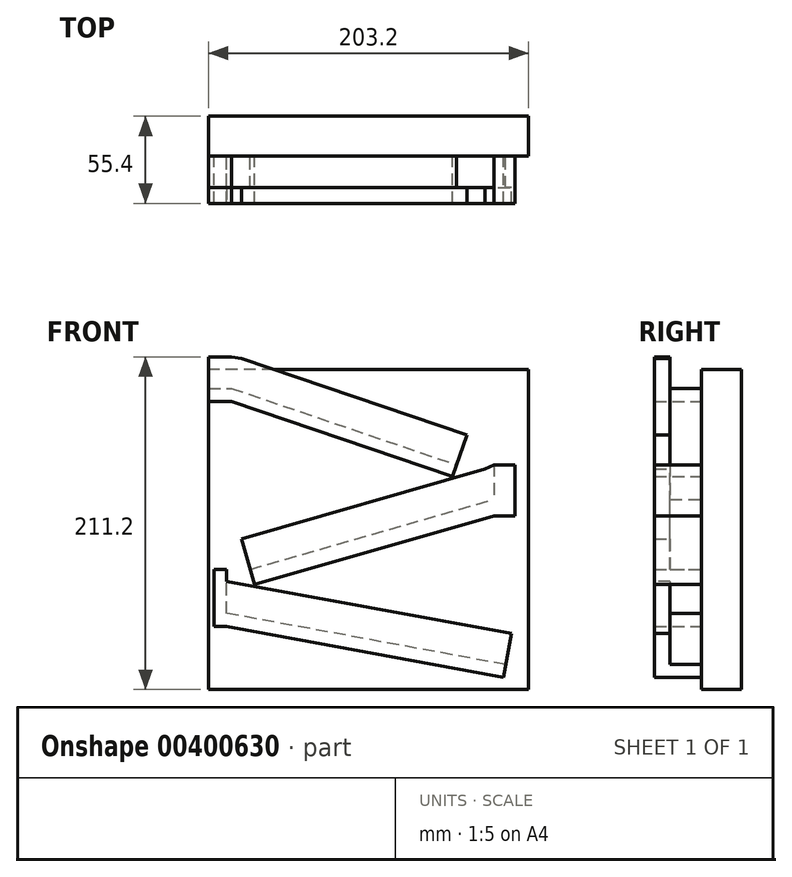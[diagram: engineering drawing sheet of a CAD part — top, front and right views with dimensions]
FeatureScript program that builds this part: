
annotation { "Feature Type Name" : "Feature", "Feature Type Description" : "" }
export const myFeature = defineFeature(function(context is Context, id is Id, definition is map)
    precondition{}
    {
        {
            var Q0;
            Q0=qCreatedBy(makeId("Front.planeOp"),FACE);
            var sketch = newSketch(context, id + "F0", { "sketchPlane" : qUnion([Q0])});
            skLineSegment(sketch, "E0.bottom", {"start": v(101.6, 101.6) * mm, "end": v(-101.6, 101.6) * mm});
            skLineSegment(sketch, "E0.top", {"start": v(101.6, -101.6) * mm, "end": v(-101.6, -101.6) * mm});
            skLineSegment(sketch, "E0.left", {"start": v(101.6, 101.6) * mm, "end": v(101.6, -101.6) * mm});
            skLineSegment(sketch, "E0.right", {"start": v(-101.6, 101.6) * mm, "end": v(-101.6, -101.6) * mm});
            skPoint(sketch, "E0.middle", {"position": v(0, 0) * mm});
            skSolve(sketch);
        }
        {
            var Q0;
            Q0 = qSketchRegion(id + "F0", true);
            extrude(context, id + "F1", {"entities" : qUnion([Q0]), "depth" : 25.4 * mm, "symmetric" : true});
        }
        {
            var Q0;
            Q0=makeQuery(id+"F1.opExtrude","CAP_FACE",FACE,{"disambiguationData":[OSD([sQuery(id+"F0.wireOp",EDGE,"E0.bottom"),sQuery(id+"F0.wireOp",EDGE,"E0.top"),sQuery(id+"F0.wireOp",EDGE,"E0.left"),sQuery(id+"F0.wireOp",EDGE,"E0.right")])],"isStart":false});
            var sketch = newSketch(context, id + "F2", { "sketchPlane" : qUnion([Q0])});
            skLineSegment(sketch, "E1", {"start": v(-101.6, 89.6) * mm, "end": v(-86.97, 89.6) * mm});
            skLineSegment(sketch, "E2", {"start": v(-86.97, 89.6) * mm, "end": v(55.97, 41) * mm});
            skLineSegment(sketch, "E3", {"start": v(55.97, 41) * mm, "end": v(53.43, 33.51) * mm});
            skLineSegment(sketch, "E4", {"start": v(53.43, 33.51) * mm, "end": v(-86.97, 81.26) * mm});
            skLineSegment(sketch, "E5", {"start": v(-86.97, 81.26) * mm, "end": v(-101.6, 81.26) * mm});
            skLineSegment(sketch, "E6", {"start": v(-101.6, 81.26) * mm, "end": v(-101.6, 89.6) * mm});
            skLineSegment(sketch, "E7", {"start": v(79.53, 41) * mm, "end": v(79.53, 8.54) * mm});
            skLineSegment(sketch, "E8", {"start": v(79.53, 8.54) * mm, "end": v(92.93, 8.54) * mm});
            skLineSegment(sketch, "E9", {"start": v(92.93, 8.54) * mm, "end": v(92.93, 41) * mm});
            skLineSegment(sketch, "E10", {"start": v(92.93, 41) * mm, "end": v(79.53, 41) * mm});
            skLineSegment(sketch, "E11", {"start": v(79.53, 8.54) * mm, "end": v(-72.35, -35.08) * mm});
            skLineSegment(sketch, "E12", {"start": v(-72.35, -35.08) * mm, "end": v(-75.13, -25.4) * mm});
            skLineSegment(sketch, "E13", {"start": v(-75.13, -25.4) * mm, "end": v(79.53, 19.02) * mm});
            skLineSegment(sketch, "E14", {"start": v(-98, -25.4) * mm, "end": v(-98, -61.62) * mm});
            skLineSegment(sketch, "E15", {"start": v(-98, -61.62) * mm, "end": v(-90.13, -61.62) * mm});
            skLineSegment(sketch, "E16", {"start": v(-90.13, -61.62) * mm, "end": v(-90.13, -25.4) * mm});
            skLineSegment(sketch, "E17", {"start": v(-90.13, -25.4) * mm, "end": v(-98, -25.4) * mm});
            skLineSegment(sketch, "E18", {"start": v(-90.13, -61.62) * mm, "end": v(85.66, -93.94) * mm});
            skLineSegment(sketch, "E19", {"start": v(85.66, -93.94) * mm, "end": v(87.14, -85.9) * mm});
            skLineSegment(sketch, "E20", {"start": v(87.14, -85.9) * mm, "end": v(-90.13, -53.3) * mm});
            skSolve(sketch);
        }
        {
            var Q0;
            Q0 = qSketchRegion(id + "F2", true);
            extrude(context, id + "F3", {"entities" : qUnion([Q0]), "operationType" : NewBodyOperationType.ADD, "depth" : 30 * mm});
        }
        {
            var Q0;
            Q0=makeQuery(id+"F3.opExtrude","SWEPT_FACE",FACE,{"disambiguationData":[OSD([sQuery(id+"F2.wireOp",EDGE,"E1")])]});
            var sketch = newSketch(context, id + "F4", { "sketchPlane" : qUnion([Q0])});
            skLineSegment(sketch, "E21.bottom", {"start": v(-101.6, -42.7) * mm, "end": v(-86.97, -42.7) * mm});
            skLineSegment(sketch, "E21.top", {"start": v(-101.6, -32.7) * mm, "end": v(-86.97, -32.7) * mm});
            skLineSegment(sketch, "E21.left", {"start": v(-101.6, -42.7) * mm, "end": v(-101.6, -32.7) * mm});
            skLineSegment(sketch, "E21.right", {"start": v(-86.97, -42.7) * mm, "end": v(-86.97, -32.7) * mm});
            skSolve(sketch);
        }
        {
            var Q0;
            Q0 = qSketchRegion(id + "F4", true);
            extrude(context, id + "F5", {"entities" : qUnion([Q0]), "operationType" : NewBodyOperationType.ADD, "depth" : 20 * mm});
        }
        {
            var Q0;
            Q0=makeQuery(id+"F3.opExtrude","SWEPT_FACE",FACE,{"disambiguationData":[OSD([sQuery(id+"F2.wireOp",EDGE,"E2")])]});
            var sketch = newSketch(context, id + "F6", { "sketchPlane" : qUnion([Q0])});
            skLineSegment(sketch, "E22.bottom", {"start": v(-111.2, -42.7) * mm, "end": v(39.79, -42.7) * mm});
            skLineSegment(sketch, "E22.top", {"start": v(-111.2, -32.7) * mm, "end": v(39.79, -32.7) * mm});
            skLineSegment(sketch, "E22.left", {"start": v(-111.2, -42.7) * mm, "end": v(-111.2, -32.7) * mm});
            skLineSegment(sketch, "E22.right", {"start": v(39.79, -42.7) * mm, "end": v(39.79, -32.7) * mm});
            skSolve(sketch);
        }
        {
            var Q0;
            Q0 = qSketchRegion(id + "F6", true);
            extrude(context, id + "F7", {"entities" : qUnion([Q0]), "operationType" : NewBodyOperationType.ADD, "depth" : 20 * mm});
        }
        {
            var Q0;
            Q0=makeQuery(id+"F7.boolean.opBoolean","MERGE",FACE,{"derivedFrom":[makeQuery(id+"F5.boolean.opBoolean","MERGE",FACE,{"derivedFrom":[makeQuery(id+"F3.opExtrude","CAP_FACE",FACE,{"disambiguationData":[OSD([sQuery(id+"F2.wireOp",EDGE,"E1"),sQuery(id+"F2.wireOp",EDGE,"E2"),sQuery(id+"F2.wireOp",EDGE,"E3"),sQuery(id+"F2.wireOp",EDGE,"E4"),sQuery(id+"F2.wireOp",EDGE,"E5"),sQuery(id+"F2.wireOp",EDGE,"E6")])],"isStart":false}),makeQuery(id+"F5.opExtrude","SWEPT_FACE",FACE,{"disambiguationData":[OSD([sQuery(id+"F4.wireOp",EDGE,"E21.bottom")])]})]}),makeQuery(id+"F7.opExtrude","SWEPT_FACE",FACE,{"disambiguationData":[OSD([sQuery(id+"F6.wireOp",EDGE,"E22.bottom")])]})]});
            var sketch = newSketch(context, id + "F8", { "sketchPlane" : qUnion([Q0])});
            skLineSegment(sketch, "E23", {"start": v(-86.97, 89.6) * mm, "end": v(-80.53, 108.54) * mm});
            skLineSegment(sketch, "E24", {"start": v(-80.53, 108.54) * mm, "end": v(-86.97, 109.6) * mm});
            skLineSegment(sketch, "E25", {"start": v(-86.97, 109.6) * mm, "end": v(-86.97, 89.6) * mm});
            skSolve(sketch);
        }
        {
            var Q0;
            Q0 = qSketchRegion(id + "F8", true);
            extrude(context, id + "F9", {"entities" : qUnion([Q0]), "operationType" : NewBodyOperationType.ADD, "oppositeDirection" : true, "depth" : 10 * mm});
        }
        {
            var Q0;
            Q0=makeQuery(id+"F3.opExtrude","SWEPT_FACE",FACE,{"disambiguationData":[OSD([sQuery(id+"F2.wireOp",EDGE,"E13")])]});
            var sketch = newSketch(context, id + "F10", { "sketchPlane" : qUnion([Q0])});
            skLineSegment(sketch, "E26.bottom", {"start": v(-79.22, -42.7) * mm, "end": v(81.69, -42.7) * mm});
            skLineSegment(sketch, "E26.top", {"start": v(-79.22, -32.7) * mm, "end": v(81.69, -32.7) * mm});
            skLineSegment(sketch, "E26.left", {"start": v(-79.22, -42.7) * mm, "end": v(-79.22, -32.7) * mm});
            skLineSegment(sketch, "E26.right", {"start": v(81.69, -42.7) * mm, "end": v(81.69, -32.7) * mm});
            skSolve(sketch);
        }
        {
            var Q0;
            Q0 = qSketchRegion(id + "F10", true);
            extrude(context, id + "F11", {"entities" : qUnion([Q0]), "operationType" : NewBodyOperationType.ADD, "depth" : 20 * mm});
        }
        {
            var Q0;
            Q0=makeQuery(id+"F3.opExtrude","SWEPT_FACE",FACE,{"disambiguationData":[OSD([sQuery(id+"F2.wireOp",EDGE,"E20")])]});
            var sketch = newSketch(context, id + "F12", { "sketchPlane" : qUnion([Q0])});
            skLineSegment(sketch, "E27.bottom", {"start": v(-79, -42.7) * mm, "end": v(101.23, -42.7) * mm});
            skLineSegment(sketch, "E27.top", {"start": v(-79, -32.7) * mm, "end": v(101.23, -32.7) * mm});
            skLineSegment(sketch, "E27.left", {"start": v(-79, -42.7) * mm, "end": v(-79, -32.7) * mm});
            skLineSegment(sketch, "E27.right", {"start": v(101.23, -42.7) * mm, "end": v(101.23, -32.7) * mm});
            skSolve(sketch);
        }
        {
            var Q0;
            Q0 = qSketchRegion(id + "F12", true);
            extrude(context, id + "F13", {"entities" : qUnion([Q0]), "operationType" : NewBodyOperationType.ADD, "depth" : 20 * mm});
        }
        {
            var Q0;
            Q0=makeQuery(id+"F11.boolean.opBoolean","MERGE",FACE,{"derivedFrom":[makeQuery(id+"F3.opExtrude","CAP_FACE",FACE,{"disambiguationData":[OSD([sQuery(id+"F2.wireOp",EDGE,"E7"),sQuery(id+"F2.wireOp",EDGE,"E8"),sQuery(id+"F2.wireOp",EDGE,"E9"),sQuery(id+"F2.wireOp",EDGE,"E10"),sQuery(id+"F2.wireOp",EDGE,"E11"),sQuery(id+"F2.wireOp",EDGE,"E12"),sQuery(id+"F2.wireOp",EDGE,"E13")])],"isStart":false}),makeQuery(id+"F11.opExtrude","SWEPT_FACE",FACE,{"disambiguationData":[OSD([sQuery(id+"F10.wireOp",EDGE,"E26.bottom")])]})]});
            var sketch = newSketch(context, id + "F14", { "sketchPlane" : qUnion([Q0])});
            skLineSegment(sketch, "E28", {"start": v(79.53, 19.02) * mm, "end": v(79.53, 41) * mm});
            skLineSegment(sketch, "E29", {"start": v(79.53, 41) * mm, "end": v(74, 38.24) * mm});
            skLineSegment(sketch, "E30", {"start": v(74, 38.24) * mm, "end": v(79.53, 19.02) * mm});
            skSolve(sketch);
        }
        {
            var Q0;
            Q0 = qSketchRegion(id + "F14", true);
            extrude(context, id + "F15", {"entities" : qUnion([Q0]), "operationType" : NewBodyOperationType.ADD, "oppositeDirection" : true, "depth" : 10 * mm});
        }
        {
            var Q0;
            Q0=makeQuery(id+"F13.boolean.opBoolean","MERGE",FACE,{"derivedFrom":[makeQuery(id+"F3.opExtrude","CAP_FACE",FACE,{"disambiguationData":[OSD([sQuery(id+"F2.wireOp",EDGE,"E14"),sQuery(id+"F2.wireOp",EDGE,"E15"),sQuery(id+"F2.wireOp",EDGE,"E16"),sQuery(id+"F2.wireOp",EDGE,"E17"),sQuery(id+"F2.wireOp",EDGE,"E18"),sQuery(id+"F2.wireOp",EDGE,"E19"),sQuery(id+"F2.wireOp",EDGE,"E20")])],"isStart":false}),makeQuery(id+"F13.opExtrude","SWEPT_FACE",FACE,{"disambiguationData":[OSD([sQuery(id+"F12.wireOp",EDGE,"E27.bottom")])]})]});
            var sketch = newSketch(context, id + "F16", { "sketchPlane" : qUnion([Q0])});
            skLineSegment(sketch, "E31", {"start": v(-90.13, -53.3) * mm, "end": v(-86.5, -33.63) * mm});
            skLineSegment(sketch, "E32", {"start": v(-86.5, -33.63) * mm, "end": v(-90.13, -32.96) * mm});
            skLineSegment(sketch, "E33", {"start": v(-90.13, -32.96) * mm, "end": v(-90.13, -53.3) * mm});
            skSolve(sketch);
        }
        {
            var Q0;
            Q0 = qSketchRegion(id + "F16", true);
            extrude(context, id + "F17", {"entities" : qUnion([Q0]), "operationType" : NewBodyOperationType.ADD, "oppositeDirection" : true, "depth" : 10 * mm});
        }
    });
